# Revit family: SPB
name_source: partatom
category: Lighting Fixtures
units: mm (PartAtom-declared; Revit-internal decimal feet)

## family parameters
Cut with Voids When Loaded = No
Host = Face
Light Source = Yes
OmniClass Number = 23.80.70.00
OmniClass Title = Lighting
Part Type = Normal
Room Calculation Point = No
Round Connector Dimension = Use Diameter
Shared = No

## types (1)
- SPB
    Apparent Load = 42 VA
    Assembly Code = D5020200
    Body Material = Paint-Carbon Black
    Color Filter = 16777215
    Default Elevation = 0"
    Description = Architectural Outdoor Lighting
    Dimming Lamp Color Temperature Shift = <None>
    Emit Shape Visible in Rendering = No
    Emit from Circle Diameter = 6"
    Frame Material = Metal-Gray
    Glass Material = Glass-Clear
    Grille material = Metal-Bronze
    Lamp = LED/COMPACT FLUORESCENT/METAL HALIDE/HIGH PRESSURE SODIUM
    Load Classification = Lighting
    Manufacturer = Architectural Area Lighting
    MasterFormat Title = Parking Lighting, Roadway Lighting, Site Lighting
    Model = SPB
    Number of Poles = 1
    OmniClass Number = 23.80.70.14.11.11
    OmniClass Title = Lighting Bollard
    Photometric Notes = More IES files download on Photometric Web Link
    Photometric Web File = SPB.IES
    Power Factor = 1
    Series = Spectra Bollard
    Shaft Height = 42"
    Tilt Angle = -90.00°
    Type Comments = Lighting Fixture
    URL = https://www.currentlighting.com
    Voltage = 120 V
    Wattage Comments = 42W
    Width = 7 1/2"

## geometry (parser evidence)
native form markers: Blend x12, Sweep x2
no freeform markers — native parametric forms only
